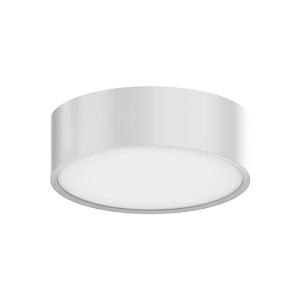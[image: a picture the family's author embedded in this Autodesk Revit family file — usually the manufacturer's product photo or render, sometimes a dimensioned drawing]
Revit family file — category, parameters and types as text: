
# Revit family: ledceilinglu-e_rd142-24w-830-wh_540001295400
name_source: partatom
category: Leuchten
revit_build: Autodesk Revit 2016 (Build: 20190508_0715(x64)
units: mm (PartAtom-declared; Revit-internal decimal feet)

## family parameters
Basisbauteil = Fläche
Beim Laden mit Abzugskörper schneiden = Nein
Bemaßung runder Anschluss = Durchmesser verwenden
Gemeinsam genutzt = Nein
Lichtquelle = Nein
Raumberechnungspunkt = Nein
Teiletyp = Normal

## types (1)
- LEDCeilingLu-E Rd142-24W-830-WH (1 x LED, 2040 lm)
    Approval mark = CE
    Beschreibung = Stylish and compact ceiling luminaire. Clean “twist-and-lock” mounting system. High quality full metal body. Low height of only 46mm. Suitable for ceiling and wall mounting.
    CIE Flux Codes = 48 79 96 100 100
    Control Gear = Electronic ballast
    Height = 100 mm  [stored 0.328084 ft]
    Hersteller = OPPLE
    Lamp Light Flux = 2040 lm
    Lamp count = 1
    Lampe = 1 x LED
    Length = 100 mm  [stored 0.328084 ft]
    Luminous efficacy = 85 lm/W
    ModVariant = Nein
    Modell = 540001295400
    Mounting Place = Wall, Ceiling
    Mounting Type = Surface mounted
    Number of Poles = 1
    OnlyDefault = Ja
    Power Factor = 1
    Product Name = LEDCeilingLu-E Rd142-24W-830-WH
    Product group = Ceiling Light Luna
    ProductGroupID = 305
    Protection Class = Protection class II
    Protection Degree = IP 20
    RLX_Detail_Level = 1
    RlxData = <blob elided: 125637 chars, md5=58e154f9>
    Scheinlast = 24 VA
    Socket = socket
    Standby Power = 0 W
    System Light Flux = 2040 lm
    System Power = 24 W
    Typenbild = luna_wh_rd142.jpg
    Typenkommentare = Product without accessories
    URL = http://relux.com
    VarID = ---
    Voltage = 230 V
    Voltage Range = 220-240 V
    Vorgabe-Ansicht = 1800 mm
    Weight = 0.00 kg
    Width = 100 mm  [stored 0.328084 ft]

note: [stored X ft] marks values corroborated as IEEE doubles in the binary element streams (Revit-internal decimal feet)

## geometry (parser evidence)
native form markers: Blend x4, Sweep x9
no freeform markers — native parametric forms only
